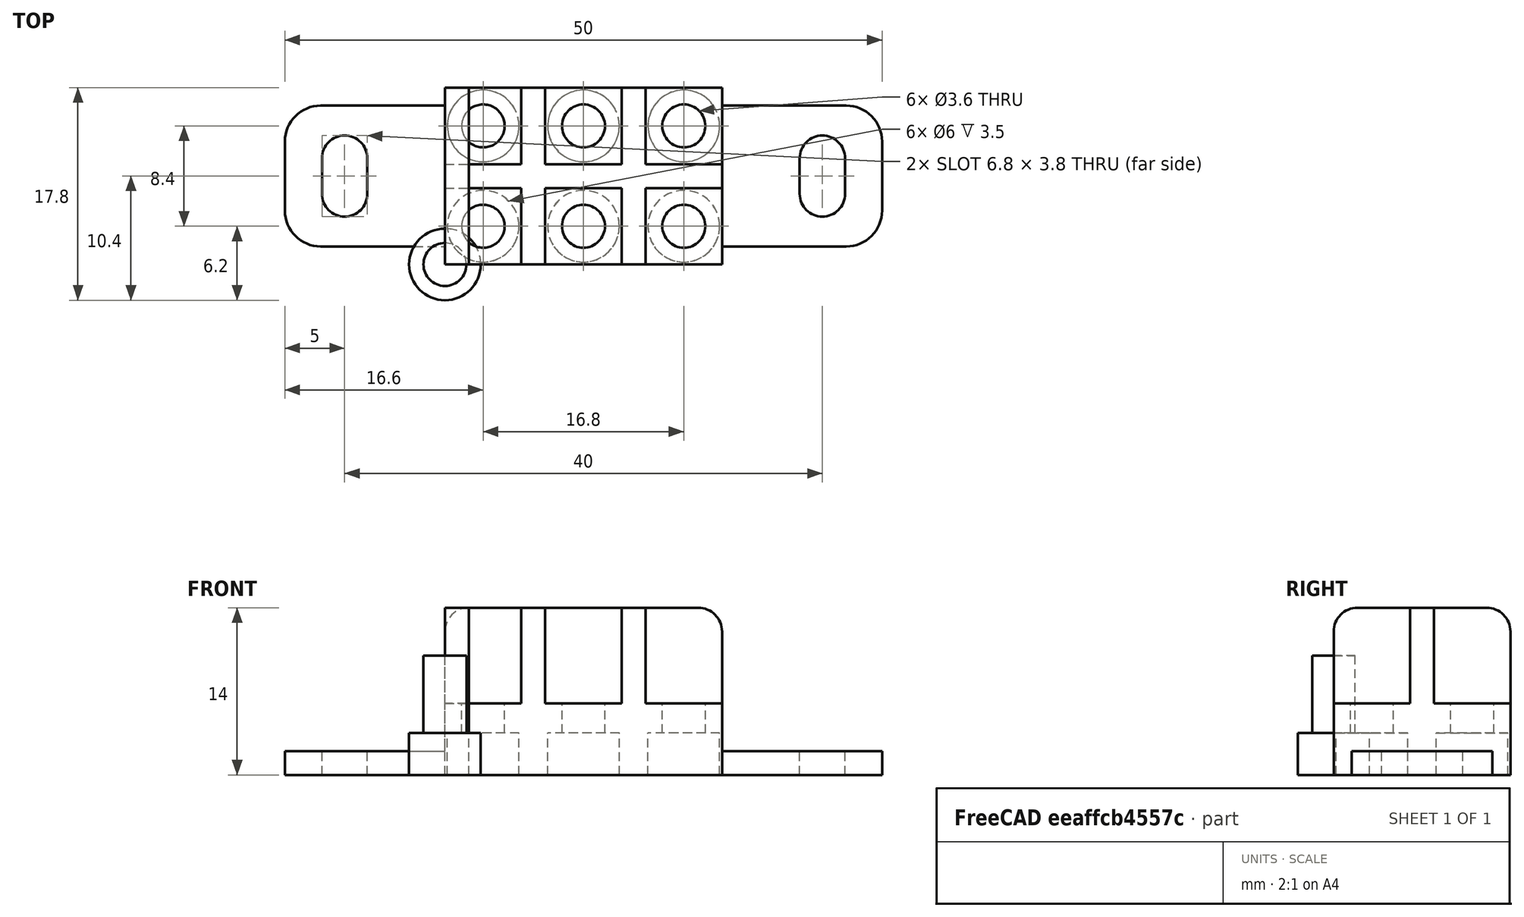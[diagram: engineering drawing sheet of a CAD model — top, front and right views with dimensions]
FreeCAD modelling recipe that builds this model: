
FCSTD DOCUMENT  (FreeCAD 0.19R)
Label: bolt_connector_plate
License: All rights reserved
LicenseURL: http://en.wikipedia.org/wiki/All_rights_reserved
objects: Part::Box×3, Part::Cylinder×2, Part::MultiFuse×2, Part::FeaturePython×2, Part::Fillet×2, Spreadsheet::Sheet×1, Part::Feature×1, Part::Cut×1, App::Part×1
note: 11 computed .brp shape members not serialized (recipe doc carries the construction recipe); baked Part::Feature solids carry a one-line shape summary decoded from their .brp

FEATURE [Part::Box] Box  label="base cube"
  AttacherType = Attacher::AttachEngine3D
  Height = 6
  Length = 23.2
  Width = 14.8
  expr: Length = <<p>>.box_x
  expr: Width = <<p>>.box_y
  expr: Height = <<p>>.box_z
FEATURE [Spreadsheet::Sheet] Spreadsheet  label="p"
  cells = A1=hole_area_r; B1(hole_area_r)==3.2mm; A2=hole_r; B2(hole_r)==1.8mm; A3=between_hole_wall; B3(between_hole_wall)==2mm; A4=between_hole_wall_z; B4(between_hole_wall_z)==8mm; A5=count_x; B5(count_x)=3; A6=count_y; B6(count_y)=2; A7=box_x; B7(box_x)==(2 * hole_area_r + between_hole_wall) * count_x - between_hole_wall; A8=box_y; B8(box_y)==(2 * hole_area_r + between_hole_wall) * count_y - between_hole_wall; A9=box_z; B9(box_z)==6mm; A10=bolt_head_r; B10(bolt_head_r)==3mm; A11=bolt_head_z; B11(bolt_head_z)==3.5mm
FEATURE [Part::Cylinder] Cylinder  label="bolt hole"
  Angle = 360
  AttacherType = Attacher::AttachEngine3D
  Height = 10
  Radius = 1.8
  expr: Radius = <<p>>.hole_r
FEATURE [Part::Cylinder] Cylinder001  label="bolt head hole"
  Angle = 360
  AttacherType = Attacher::AttachEngine3D
  Height = 3.5
  Radius = 3
  expr: Height = <<p>>.bolt_head_z
  expr: Radius = <<p>>.bolt_head_r
FEATURE [Part::Box] Box001  label="wall along x"
  AttacherType = Attacher::AttachEngine3D
  Height = 14
  Length = 23.2
  Placement = pos=(0,6.4,0) rot=(0,0,1;0rad)
  Width = 2
  expr: .Placement.Base.y = (<<base cube>>.Width - <<p>>.between_hole_wall) / 2
  expr: Length = <<base cube>>.Length
  expr: Width = <<p>>.between_hole_wall
  expr: Height = <<p>>.box_z + <<p>>.between_hole_wall_z
FEATURE [Part::Box] Box002  label="wall along y"
  AttacherType = Attacher::AttachEngine3D
  Height = 14
  Length = 2
  Width = 14.8
  expr: Height = <<p>>.box_z + <<p>>.between_hole_wall_z
  expr: Width = <<base cube>>.Width
  expr: Length = <<p>>.between_hole_wall
FEATURE [Part::MultiFuse] Fusion  label="bolt extract fusion"
  Shapes = -> [Cylinder,Cylinder001]
FEATURE [Part::FeaturePython] Array001  label="bolt extract fusion array"  # Draft array (typed FeaturePython)
  Angle = 360
  ArrayType = 0
  Axis = (0,0,1)
  Base = -> Fusion
  Center = (0,0,0)
  Count = 6
  ExpandArray = false
  Fuse = false
  IntervalAxis = (0,0,0)
  IntervalX = (8.4,0,0)
  IntervalY = (0,8.4,0)
  IntervalZ = (0,0,100)
  NumberCircles = 3
  NumberPolar = 5
  NumberX = 3
  NumberY = 2
  NumberZ = 1
  Placement = pos=(3.2,3.2,0) rot=(0,0,1;0rad)
  PlacementList = 6 placements: [(0,0,0),(0,8.4,0),(8.4,0,0),(8.4,8.4,0),(16.8,0,0),(16.8,8.4,0)]
  RadialDistance = 50
  ScaleList = (6) [(1,1,1),(1,1,1),(1,1,1),(1,1,1),(1,1,1),(1,1,1)]
  Symmetry = 1
  TangentialDistance = 25
  expr: .IntervalY.y = <<p>>.hole_area_r * 2 + <<p>>.between_hole_wall
  expr: .IntervalX.x = <<p>>.hole_area_r * 2 + <<p>>.between_hole_wall
  expr: NumberY = <<p>>.count_y
  expr: NumberX = <<p>>.count_x
  expr: .Placement.Base.y = <<p>>.hole_area_r
  expr: .Placement.Base.x = <<p>>.hole_area_r
FEATURE [Part::Fillet] Fillet  label="wall along x fillet"
  Base = -> Box001
  Edges = 2 edges r=2: [Edge2,Edge6]
FEATURE [Part::Fillet] Fillet001  label="wall along y fillet"
  Base = -> Box002
  Edges = 2 edges r=2: [Edge10,Edge12]
FEATURE [Part::FeaturePython] Array  label="wall along y array"  # Draft array (typed FeaturePython)
  Angle = 360
  ArrayType = 0
  Axis = (0,0,1)
  Base = -> Fillet001
  Center = (0,0,0)
  Count = 2
  ExpandArray = false
  Fuse = false
  IntervalAxis = (0,0,0)
  IntervalX = (8.4,0,0)
  IntervalY = (0,100,0)
  IntervalZ = (0,0,100)
  NumberCircles = 3
  NumberPolar = 5
  NumberX = 2
  NumberY = 1
  NumberZ = 1
  Placement = pos=(6.4,0,0) rot=(0,0,1;0rad)
  PlacementList = 2 placements: [(0,0,0),(8.4,0,0)]
  RadialDistance = 50
  ScaleList = (2) [(1,1,1),(1,1,1)]
  Symmetry = 1
  TangentialDistance = 25
  expr: .Placement.Base.x = <<p>>.hole_area_r * 2
  expr: NumberX = <<p>>.count_x - 1
  expr: .IntervalX.x = 2 * <<p>>.hole_area_r + <<p>>.between_hole_wall
FEATURE [Part::Feature] Cut003001  label="attach plane x dir001"
  Placement = pos=(-13.4,1.5,0) rot=(0,0,1;0rad)
  shape: bbox 50 x 11.8 x 2 mm, 18 faces (baked)
FEATURE [Part::MultiFuse] Fusion001  label="body fusion"
  Shapes = -> [Box,Array,Fillet,Cut003001]
FEATURE [Part::Cut] Cut  label="plate cut"
  Base = -> Fusion001
  Tool = -> Array001
FEATURE [App::Part] Part
  Group = -> [Cut]
  Origin = -> Origin
